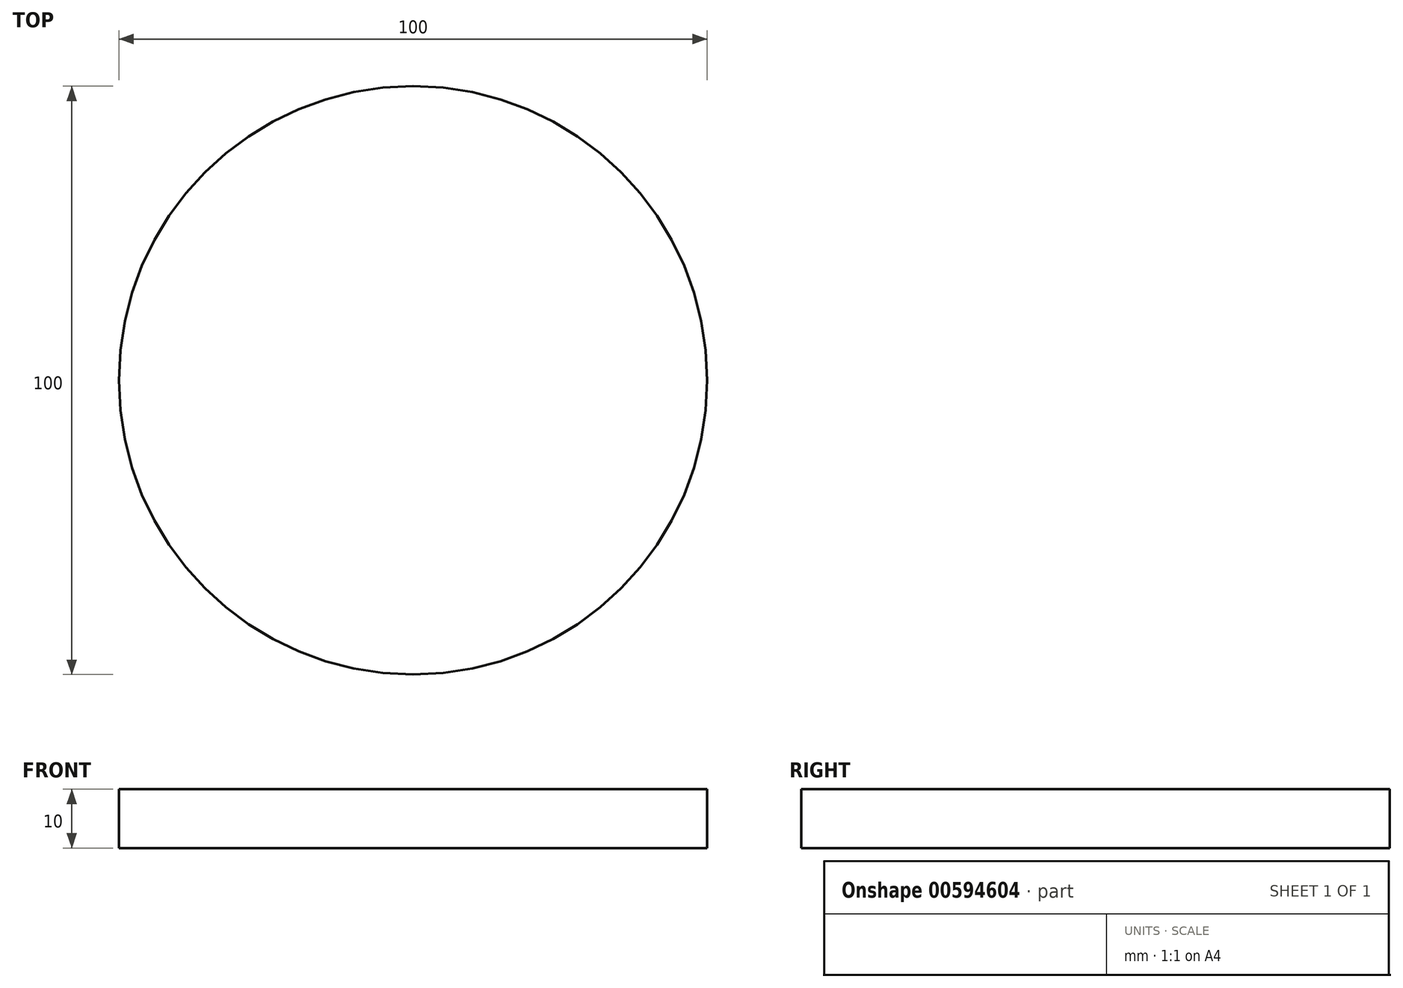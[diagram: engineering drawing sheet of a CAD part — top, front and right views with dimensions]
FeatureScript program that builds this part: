
annotation { "Feature Type Name" : "Feature", "Feature Type Description" : "" }
export const myFeature = defineFeature(function(context is Context, id is Id, definition is map)
    precondition{}
    {
        {
            var Q0;
            Q0=qCreatedBy(makeId("Top.planeOp"),FACE);
            var sketch = newSketch(context, id + "F0", { "sketchPlane" : qUnion([Q0])});
            skCircle(sketch, "E0", {"center": v(0, 0) * mm, "radius": 275 * mm});
            skSolve(sketch);
        }
        {
            var Q0;
            Q0 = qSketchRegion(id + "F0", true);
            extrude(context, id + "F1", {"entities" : qUnion([Q0]), "depth" : 10 * mm, "offsetDistance" : 25 * mm});
        }
        {
            var Q0;
            Q0=makeQuery(id+"F1.opExtrude","CAP_FACE",FACE,{"disambiguationData":[OSD([sQuery(id+"F0.wireOp",EDGE,"E0")])],"isStart":false});
            var sketch = newSketch(context, id + "F2", { "sketchPlane" : qUnion([Q0])});
            skCircle(sketch, "E1", {"center": v(-100, 0) * mm, "radius": 50 * mm});
            skSolve(sketch);
        }
        {
            var Q0;
            Q0 = qSketchRegion(id + "F2", true);
            extrude(context, id + "F3", {"entities" : qUnion([Q0]), "operationType" : NewBodyOperationType.REMOVE, "oppositeDirection" : true, "depth" : 25 * mm, "offsetDistance" : 25 * mm});
        }
        {
            var Q0;
            Q0=makeQuery(id+"F1.opExtrude","CAP_FACE",FACE,{"disambiguationData":[OSD([sQuery(id+"F0.wireOp",EDGE,"E0")])],"isStart":false});
            var sketch = newSketch(context, id + "F4", { "sketchPlane" : qUnion([Q0])});
            skCircle(sketch, "E2", {"center": v(0, -180) * mm, "radius": 50 * mm});
            skCircle(sketch, "E3.MirrorC", {"center": v(0, 180) * mm, "radius": 50 * mm});
            skSolve(sketch);
        }
        {
            var Q0;
            Q0=makeQuery(id+"F4.imprint","IMPRINT",FACE,{"disambiguationData":[TD([[makeQuery(id+"F4.imprint","IMPRINT",EDGE,{"derivedFrom":sQuery(id+"F4.wireOp",EDGE,"E3.MirrorC")}),-1.0]])]});
            var Q1;
            Q1=makeQuery(id+"F4.imprint","IMPRINT",FACE,{"disambiguationData":[TD([[makeQuery(id+"F4.imprint","IMPRINT",EDGE,{"derivedFrom":sQuery(id+"F4.wireOp",EDGE,"E2")}),1.0]])]});
            extrude(context, id + "F5", {"entities" : qUnion([Q0, Q1]), "operationType" : NewBodyOperationType.REMOVE, "oppositeDirection" : true, "depth" : 25 * mm, "offsetDistance" : 25 * mm});
        }
        {
            var Q0;
            Q0=makeQuery(id+"F1.opExtrude","CAP_FACE",FACE,{"disambiguationData":[OSD([sQuery(id+"F0.wireOp",EDGE,"E0")])],"isStart":false});
            var sketch = newSketch(context, id + "F6", { "sketchPlane" : qUnion([Q0])});
            skCircle(sketch, "E4", {"center": v(200, 0) * mm, "radius": 47.81 * mm});
            skSolve(sketch);
        }
        {
            var Q0;
            Q0=makeQuery(id+"F6.imprint","IMPRINT",FACE,{"disambiguationData":[TD([[makeQuery(id+"F6.imprint","IMPRINT",EDGE,{"derivedFrom":sQuery(id+"F6.wireOp",EDGE,"E4")}),1.0]])]});
            extrude(context, id + "F7", {"entities" : qUnion([Q0]), "operationType" : NewBodyOperationType.REMOVE, "endBound" : BoundingType.THROUGH_ALL, "oppositeDirection" : true, "depth" : 25 * mm, "offsetDistance" : 25 * mm});
        }
        {
            var Q0;
            Q0=makeQuery(id+"F1.opExtrude","CAP_FACE",FACE,{"disambiguationData":[OSD([sQuery(id+"F0.wireOp",EDGE,"E0")])],"isStart":false});
            var sketch = newSketch(context, id + "F8", { "sketchPlane" : qUnion([Q0])});
            skCircle(sketch, "E5", {"center": v(153.7, 124.28) * mm, "radius": 25 * mm});
            skSolve(sketch);
        }
        {
            var Q0;
            Q0 = qSketchRegion(id + "F8", true);
            extrude(context, id + "F9", {"entities" : qUnion([Q0]), "operationType" : NewBodyOperationType.REMOVE, "oppositeDirection" : true, "depth" : 25 * mm, "offsetDistance" : 25 * mm});
        }
        {
            var Q0;
            Q0=makeQuery(id+"F1.opExtrude","CAP_FACE",FACE,{"disambiguationData":[OSD([sQuery(id+"F0.wireOp",EDGE,"E0")])],"isStart":false});
            var sketch = newSketch(context, id + "F10", { "sketchPlane" : qUnion([Q0])});
            skCircle(sketch, "E6", {"center": v(161.17, -132.83) * mm, "radius": 12.5 * mm});
            skSolve(sketch);
        }
        {
            var Q0;
            Q0=makeQuery(id+"F10.imprint","IMPRINT",FACE,{"disambiguationData":[TD([[makeQuery(id+"F10.imprint","IMPRINT",EDGE,{"derivedFrom":sQuery(id+"F10.wireOp",EDGE,"E6")}),1.0]])]});
            extrude(context, id + "F11", {"entities" : qUnion([Q0]), "operationType" : NewBodyOperationType.REMOVE, "oppositeDirection" : true, "depth" : 25 * mm, "offsetDistance" : 25 * mm});
        }
    });
